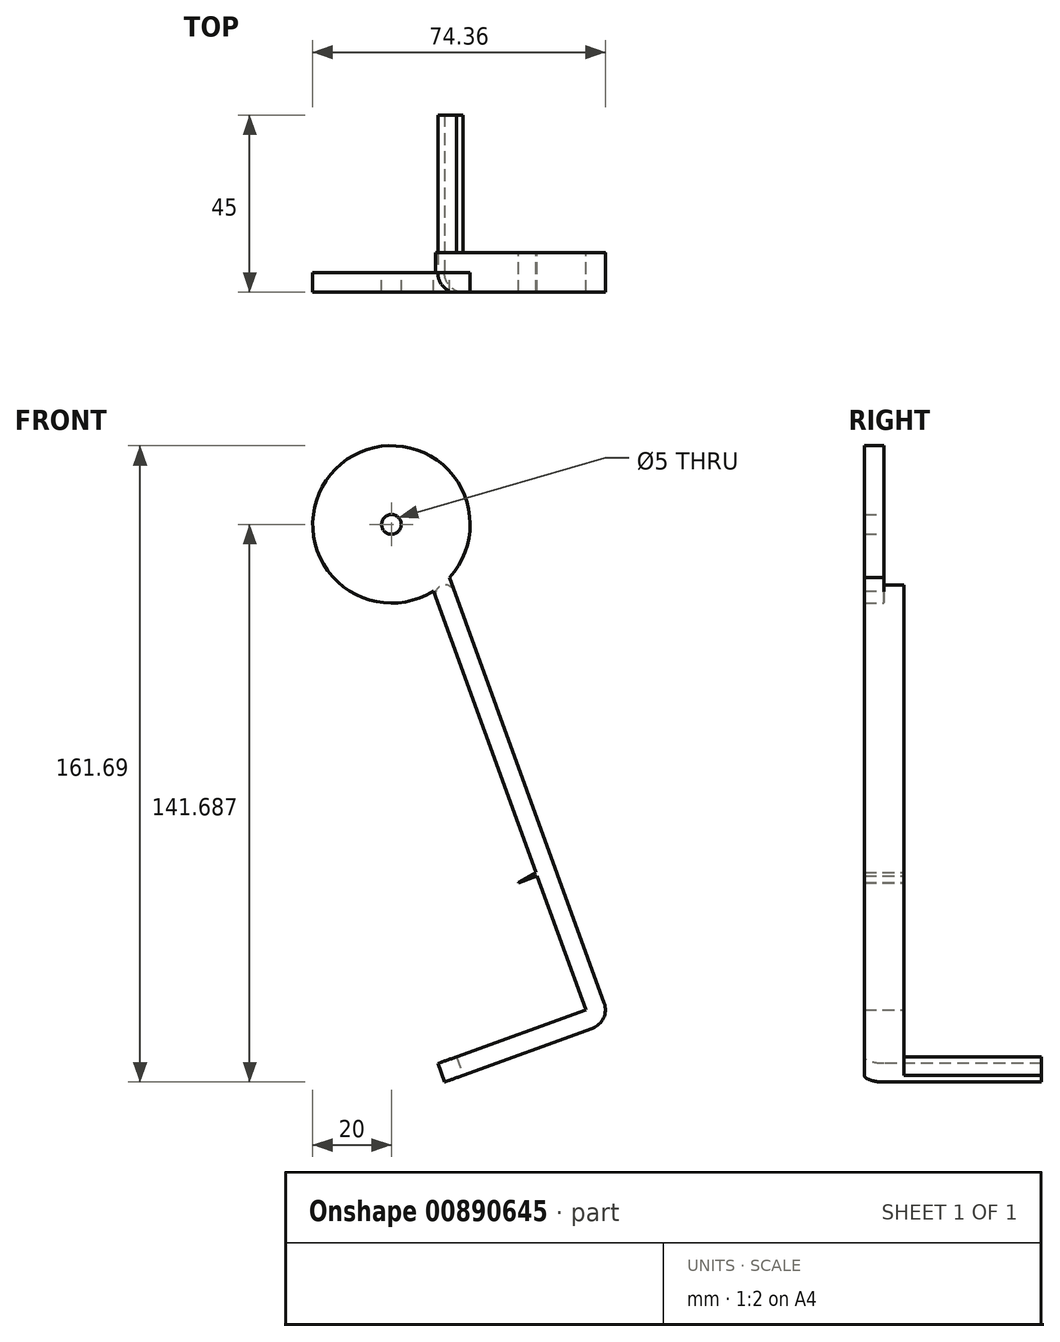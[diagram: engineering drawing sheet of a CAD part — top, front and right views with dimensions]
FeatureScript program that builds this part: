
annotation { "Feature Type Name" : "Feature", "Feature Type Description" : "" }
export const myFeature = defineFeature(function(context is Context, id is Id, definition is map)
    precondition{}
    {
        {
            var Q0;
            Q0=qCreatedBy(makeId("Front.planeOp"),FACE);
            var sketch = newSketch(context, id + "F0", { "sketchPlane" : qUnion([Q0])});
            skCircle(sketch, "E0", {"center": v(0, 33.82) * mm, "radius": 2.5 * mm});
            skLineSegment(sketch, "E1", {"start": v(0, 70.54) * mm, "end": v(0, -41.15) * mm, "construction": true});
            skCircle(sketch, "E2", {"center": v(0, 33.82) * mm, "radius": 20 * mm});
            skLineSegment(sketch, "E3.MirrorCS", {"start": v(37, -55.54) * mm, "end": v(32.3, -57.25) * mm});
            skLineSegment(sketch, "E4.MirrorCS", {"start": v(31.97, -56.3) * mm, "end": v(36.66, -54.6) * mm});
            skLineSegment(sketch, "E5.MirrorCS", {"start": v(32.3, -57.25) * mm, "end": v(31.97, -56.3) * mm});
            skLineSegment(sketch, "E6", {"start": v(51.07, -94.19) * mm, "end": v(55.77, -92.48) * mm});
            skLineSegment(sketch, "E7", {"start": v(51.07, -94.19) * mm, "end": v(13.49, -107.87) * mm});
            skLineSegment(sketch, "E8", {"start": v(13.49, -107.87) * mm, "end": v(11.78, -103.17) * mm});
            skLineSegment(sketch, "E9", {"start": v(11.78, -103.17) * mm, "end": v(49.36, -89.49) * mm});
            skLineSegment(sketch, "E10", {"start": v(49.36, -89.49) * mm, "end": v(37, -55.54) * mm});
            skLineSegment(sketch, "E11", {"start": v(49.36, -89.49) * mm, "end": v(51.07, -94.19) * mm});
            skLineSegment(sketch, "E12", {"start": v(36.66, -54.6) * mm, "end": v(37, -55.54) * mm});
            skLineSegment(sketch, "E13", {"start": v(55.77, -92.48) * mm, "end": v(14.73, 20.29) * mm});
            skLineSegment(sketch, "E14", {"start": v(36.66, -54.6) * mm, "end": v(10.65, 16.89) * mm});
            skLineSegment(sketch, "E15", {"start": v(16.47, -101.46) * mm, "end": v(18.18, -106.16) * mm});
            skSolve(sketch);
        }
        {
            var Q0;
            Q0=makeQuery(id+"F0.imprint","IMPRINT",FACE,{"disambiguationData":[TD([[makeQuery(id+"F0.imprint","IMPRINT",EDGE,{"derivedFrom":sQuery(id+"F0.wireOp",EDGE,"E0")}),-1.0]])]});
            var Q1;
            {var subQ0=sQuery(id+"F0.wireOp",EDGE,"d7889cdd-38ed-4d9a-b66e-05a1bf1b86fb1.MirrorCS");Q1=makeQuery(id+"F0.imprint","IMPRINT",FACE,{"disambiguationData":[TD([[makeQuery(id+"F0.imprint","IMPRINT",EDGE,{"derivedFrom":subQ0}),1.0]])]});}
            var Q2;
            {var subQ5=sQuery(id+"F0.wireOp",EDGE,"d7889cdd-38ed-4d9a-b66e-05a1bf1b86fb3.MirrorCS");Q2=makeQuery(id+"F0.imprint","IMPRINT",FACE,{"disambiguationData":[TD([[makeQuery(id+"F0.imprint","IMPRINT",EDGE,{"derivedFrom":subQ5}),1.0]])]});}
            var Q3;
            {var subQ3=sQuery(id+"F0.wireOp",EDGE,"d7889cdd-38ed-4d9a-b66e-05a1bf1b86fb3.MirrorCS");Q3=makeQuery(id+"F0.imprint","IMPRINT",FACE,{"disambiguationData":[TD([[makeQuery(id+"F0.imprint","IMPRINT",EDGE,{"derivedFrom":subQ3}),-1.0]])]});}
            var Q4;
            {var subQ0=sQuery(id+"F0.wireOp",EDGE,"E7");Q4=makeQuery(id+"F0.imprint","IMPRINT",FACE,{"disambiguationData":[TD([[makeQuery(id+"F0.imprint","IMPRINT",EDGE,{"derivedFrom":subQ0}),-1.0]])]});}
            var Q5;
            {var subQ0=sQuery(id+"F0.wireOp",EDGE,"E3.MirrorCS");Q5=makeQuery(id+"F0.imprint","IMPRINT",FACE,{"disambiguationData":[TD([[makeQuery(id+"F0.imprint","IMPRINT",EDGE,{"derivedFrom":subQ0}),-1.0]])]});}
            var Q6;
            Q6=makeQuery(id+"F0.imprint","IMPRINT",FACE,{"disambiguationData":[TD([[makeQuery(id+"F0.imprint","IMPRINT",EDGE,{"derivedFrom":sQuery(id+"F0.wireOp",EDGE,"E6")}),1.0]])]});
            extrude(context, id + "F1", {"entities" : qUnion([Q0, Q1, Q2, Q3, Q4, Q5, Q6]), "depth" : 5 * mm, "offsetDistance" : 25 * mm});
        }
        {
            var Q0;
            {var subQ1=sQuery(id+"F0.wireOp",EDGE,"d7889cdd-38ed-4d9a-b66e-05a1bf1b86fb1.MirrorCS");Q0=makeQuery(id+"F0.imprint","IMPRINT",FACE,{"disambiguationData":[TD([[makeQuery(id+"F0.imprint","IMPRINT",EDGE,{"derivedFrom":subQ1}),1.0]])]});}
            var Q1;
            Q1=makeQuery(id+"F0.imprint","IMPRINT",FACE,{"disambiguationData":[TD([[makeQuery(id+"F0.imprint","IMPRINT",EDGE,{"derivedFrom":sQuery(id+"F0.wireOp",EDGE,"E3.MirrorCS")}),-1.0]])]});
            var Q2;
            Q2=makeQuery(id+"F0.imprint","IMPRINT",FACE,{"disambiguationData":[TD([[makeQuery(id+"F0.imprint","IMPRINT",EDGE,{"derivedFrom":sQuery(id+"F0.wireOp",EDGE,"E6")}),1.0]])]});
            var Q3;
            {var subQ0=sQuery(id+"F0.wireOp",EDGE,"E11");Q3=makeQuery(id+"F0.imprint","IMPRINT",FACE,{"disambiguationData":[TD([[makeQuery(id+"F0.imprint","IMPRINT",EDGE,{"derivedFrom":subQ0}),-1.0]])]});}
            extrude(context, id + "F2", {"entities" : qUnion([Q0, Q1, Q2, Q3]), "operationType" : NewBodyOperationType.ADD, "oppositeDirection" : true, "depth" : 5 * mm, "offsetDistance" : 25 * mm});
        }
        {
            var Q0;
            {var subQ0=sQuery(id+"F0.wireOp",EDGE,"E13");var subQ1=sQuery(id+"F0.wireOp",EDGE,"E6");Q0=makeQuery(id+"F2.boolean.opBoolean","MERGE",EDGE,{"derivedFrom":[makeQuery(id+"F1.opExtrude","SWEPT_EDGE",EDGE,{"disambiguationData":[OSD([subQ1,subQ0])]}),makeQuery(id+"F2.opExtrude","SWEPT_EDGE",EDGE,{"disambiguationData":[OSD([subQ1,subQ0])]})]});}
            var Q1;
            Q1=makeQuery(id+"F1.opExtrude","CAP_EDGE",EDGE,{"disambiguationData":[OSD([sQuery(id+"F0.wireOp",EDGE,"E8")])],"isStart":false});
            fillet(context, id + "F3", {"entities" : qUnion([Q0, Q1]), "radius" : 5 * mm, "tangentPropagation" : true, "allowEdgeOverflow" : false});
        }
        {
            var Q0;
            Q0=makeQuery(id+"F2.opExtrude","SWEPT_EDGE",EDGE,{"disambiguationData":[OSD([sQuery(id+"F0.wireOp",EDGE,"E2"),sQuery(id+"F0.wireOp",EDGE,"d7889cdd-38ed-4d9a-b66e-05a1bf1b86fb1.MirrorCS")])]});
            var Q1;
            Q1=makeQuery(id+"F2.opExtrude","SWEPT_EDGE",EDGE,{"disambiguationData":[OSD([sQuery(id+"F0.wireOp",EDGE,"E2"),sQuery(id+"F0.wireOp",EDGE,"d7889cdd-38ed-4d9a-b66e-05a1bf1b86fb7.MirrorCS")])]});
            fillet(context, id + "F4", {"entities" : qUnion([Q0, Q1]), "radius" : 2.5 * mm, "tangentPropagation" : true, "allowEdgeOverflow" : false});
        }
        {
            var Q0;
            {var subQ0=sQuery(id+"F0.wireOp",EDGE,"E5.MirrorCS");var subQ1=sQuery(id+"F0.wireOp",EDGE,"E4.MirrorCS");Q0=makeQuery(id+"F2.boolean.opBoolean","MERGE",EDGE,{"derivedFrom":[makeQuery(id+"F1.opExtrude","SWEPT_EDGE",EDGE,{"disambiguationData":[OSD([subQ1,subQ0])]}),makeQuery(id+"F2.opExtrude","SWEPT_EDGE",EDGE,{"disambiguationData":[OSD([subQ1,subQ0])]})]});}
            chamfer(context, id + "F5", {"entities" : qUnion([Q0]), "chamferType" : ChamferType.OFFSET_ANGLE, "width" : 5 * mm, "oppositeDirection" : true, "angle" : 10 * degree, "tangentPropagation" : true});
        }
        {
            var Q0;
            {var subQ0=sQuery(id+"F0.wireOp",EDGE,"E8");Q0=makeQuery(id+"F0.imprint","IMPRINT",FACE,{"disambiguationData":[TD([[makeQuery(id+"F0.imprint","IMPRINT",EDGE,{"derivedFrom":subQ0}),-1.0]])]});}
            extrude(context, id + "F6", {"entities" : qUnion([Q0]), "operationType" : NewBodyOperationType.ADD, "oppositeDirection" : true, "depth" : 40 * mm, "offsetDistance" : 25 * mm});
        }
    });
